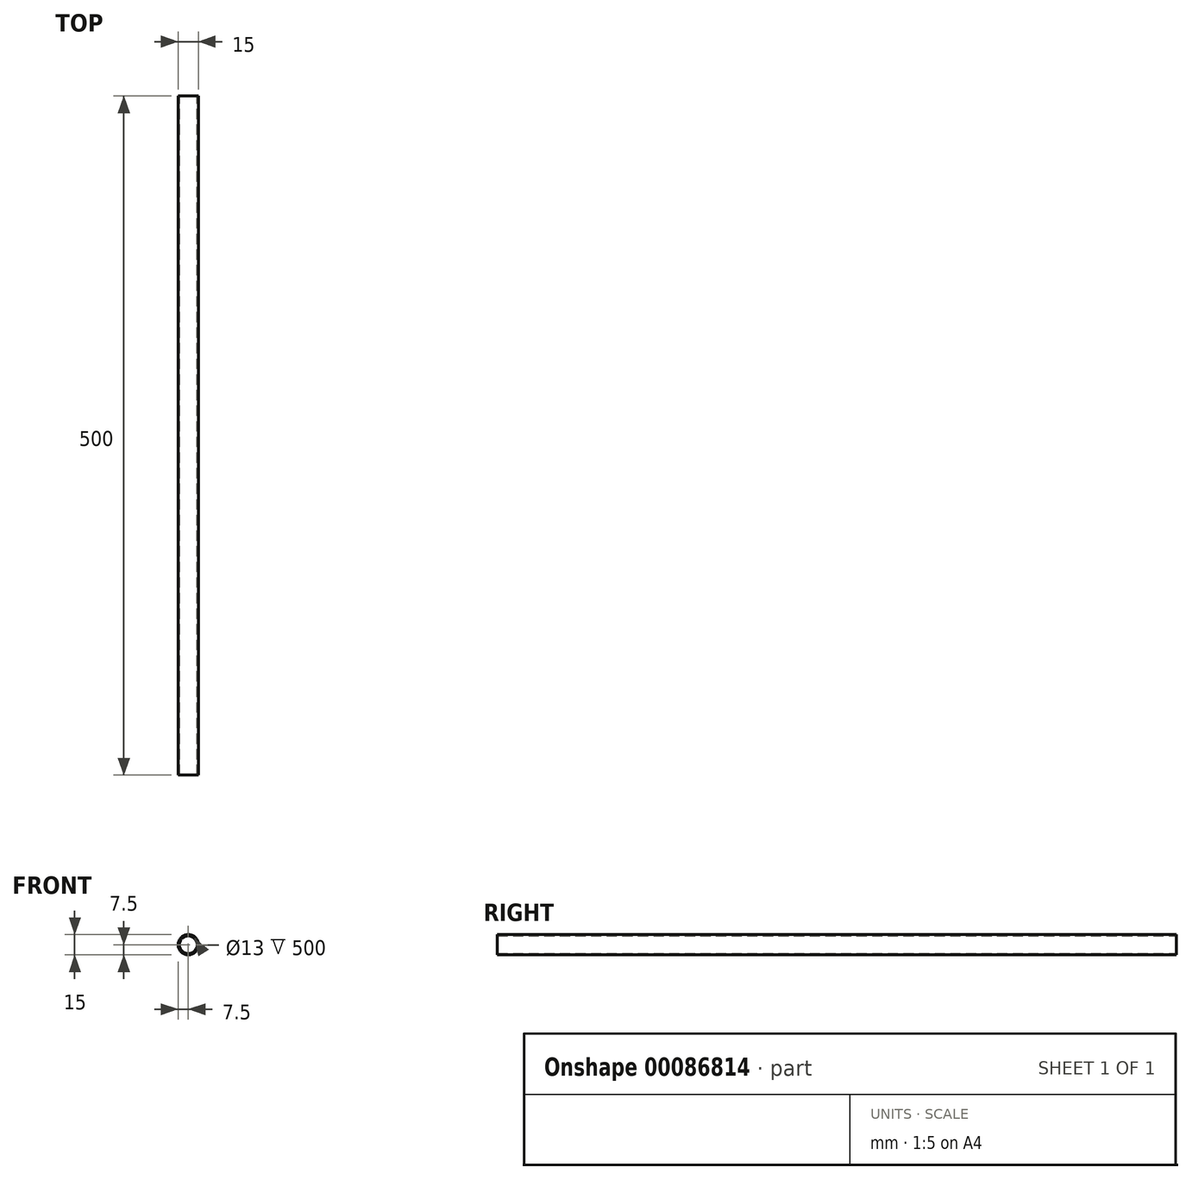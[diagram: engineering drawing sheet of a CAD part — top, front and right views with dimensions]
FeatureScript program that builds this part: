
annotation { "Feature Type Name" : "Feature", "Feature Type Description" : "" }
export const myFeature = defineFeature(function(context is Context, id is Id, definition is map)
    precondition{}
    {
        {
            assignVariable(context, id + "F0", {"name" : "tube_l", "anyValue" : 500});
        }
        {
            var Q0;
            Q0=qCreatedBy(makeId("Front.planeOp"),FACE);
            var sketch = newSketch(context, id + "F1", { "sketchPlane" : qUnion([Q0])});
            skCircle(sketch, "E0", {"center": v(0, 0) * mm, "radius": 7.5 * mm});
            skCircle(sketch, "E1.0", {"center": v(0, 0) * mm, "radius": 6.5 * mm});
            skSolve(sketch);
        }
        {
            var Q0;
            Q0 = qSketchRegion(id + "F1", true);
            extrude(context, id + "F2", {"entities" : qUnion([Q0]), "depth" : (getVariable(context, 'tube_l')) * mm});
        }
    });
